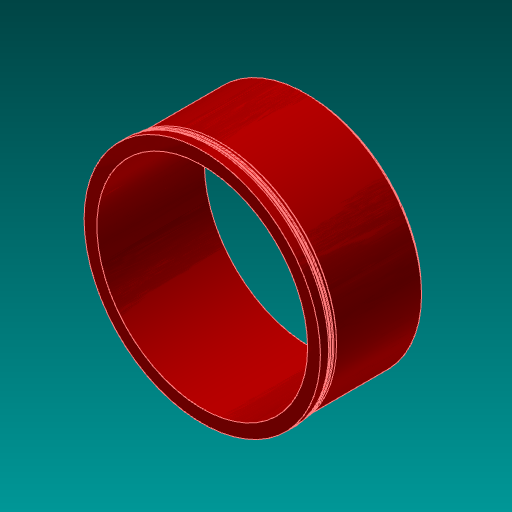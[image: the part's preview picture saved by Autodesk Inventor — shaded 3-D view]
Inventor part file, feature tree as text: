
AUTODESK INVENTOR PART (.ipt)
format: ipt  version: 2017.3 (Build 213256000, 256)  size: 226,304 bytes
history: native  units: in
note: dims shown in document units (in); Inventor stores cm internally (conversion verified against a paired STEP export)
features: extrude x4, sketch x4, chamfer x3, fillet x1, revolve x1
ambient origin geometry x8: Origin, YZ Plane, XZ Plane, XY Plane, X Axis, Y Axis, Z Axis, Center Point
bodies: Solid1 (feature_tree)
feature tree (13):
  extrude  "Extrusion1"  Depth=27.0in
  sketch  "Sketch2"  dims[d2=12.0in d3=0.0in d4=27.23in]
  extrude  "Extrusion2"  Depth=12.0in
  extrude  "Extrusion3"  Depth=1.0in TaperAngle=0.0deg
  chamfer  "Chamfer1"  Distance=1.0in
  extrude  "Extrusion4"  Depth=0.1875in TaperAngle=45.0deg
  fillet  "Fillet1"  Radius=25.98in
  chamfer  "Chamfer2"  Distance=0.5in
  chamfer  "Chamfer3"  Distance=0.0312in
  revolve  "Revolution1"  Angle=45.0deg
  sketch  "Sketch1"  dims[d0=24.5in d1=27.0in]
  sketch  "Sketch3"  dims[d5=27.48in d6=2.0in d7=0.0in d8=1.0in d9=0.0in]
  sketch  "Sketch4"  dims[d10=0.115in d11=0.125in d12=45.0deg d13=25.98in d14=0.5in d15=0.0in d16=0.0312in d17=0.0312in d18=0.125in d19=45.0deg d20=0.0312in d21=0.125in d22=45.0deg d23=0.4375in d24=0.125in d25=0.1875in d26=1.25in d27=45.0deg d28=90.0deg]
